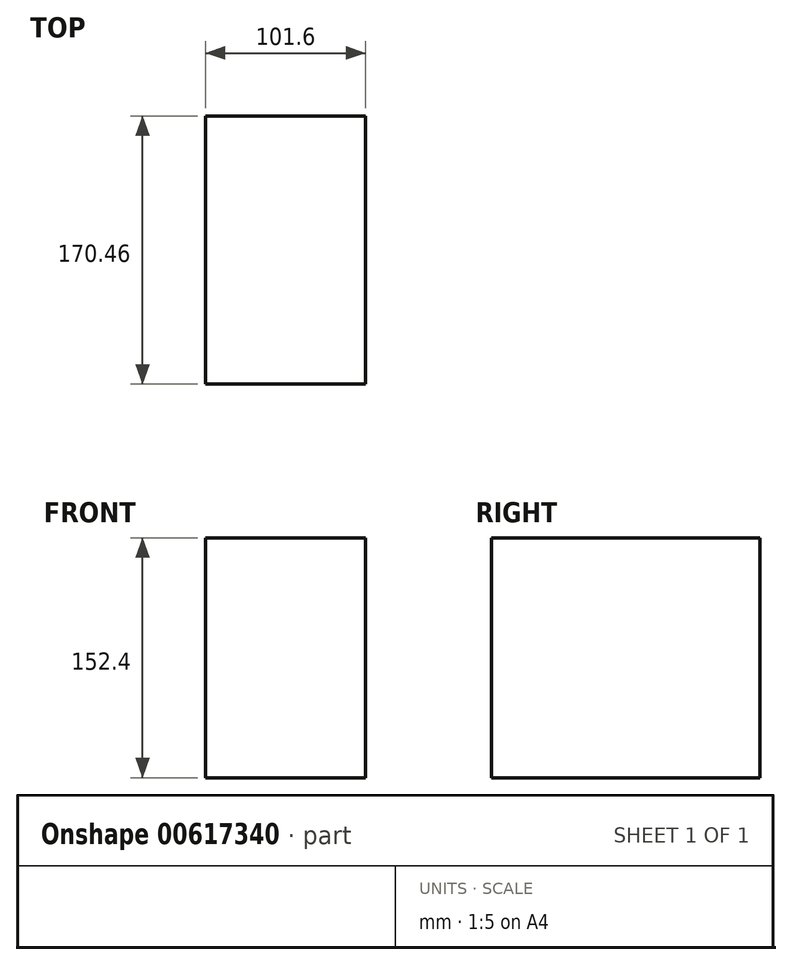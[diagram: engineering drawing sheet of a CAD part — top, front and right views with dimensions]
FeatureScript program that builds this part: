
annotation { "Feature Type Name" : "Feature", "Feature Type Description" : "" }
export const myFeature = defineFeature(function(context is Context, id is Id, definition is map)
    precondition{}
    {
        {
            var Q0;
            Q0=qCreatedBy(makeId("Top.planeOp"),FACE);
            var sketch = newSketch(context, id + "F0", { "sketchPlane" : qUnion([Q0])});
            skLineSegment(sketch, "E0", {"start": v(-57.64, 0) * mm, "end": v(-57.64, 85.3) * mm});
            skLineSegment(sketch, "E1", {"start": v(-57.64, 85.3) * mm, "end": v(43.96, 85.3) * mm});
            skLineSegment(sketch, "E2", {"start": v(43.96, 85.3) * mm, "end": v(43.96, -85.16) * mm});
            skLineSegment(sketch, "E3", {"start": v(43.96, -85.16) * mm, "end": v(-57.64, -85.16) * mm});
            skLineSegment(sketch, "E4", {"start": v(-57.64, -85.16) * mm, "end": v(-57.64, 0) * mm});
            skSolve(sketch);
        }
        {
            var Q0;
            Q0=makeQuery(id+"F0.imprint","IMPRINT",FACE,{"disambiguationData":[TD([[makeQuery(id+"F0.imprint","IMPRINT",EDGE,{"derivedFrom":sQuery(id+"F0.wireOp",EDGE,"E0")}),-1.0]])]});
            extrude(context, id + "F1", {"entities" : qUnion([Q0]), "depth" : 152.4 * mm, "offsetDistance" : 25.4 * mm});
        }
    });
